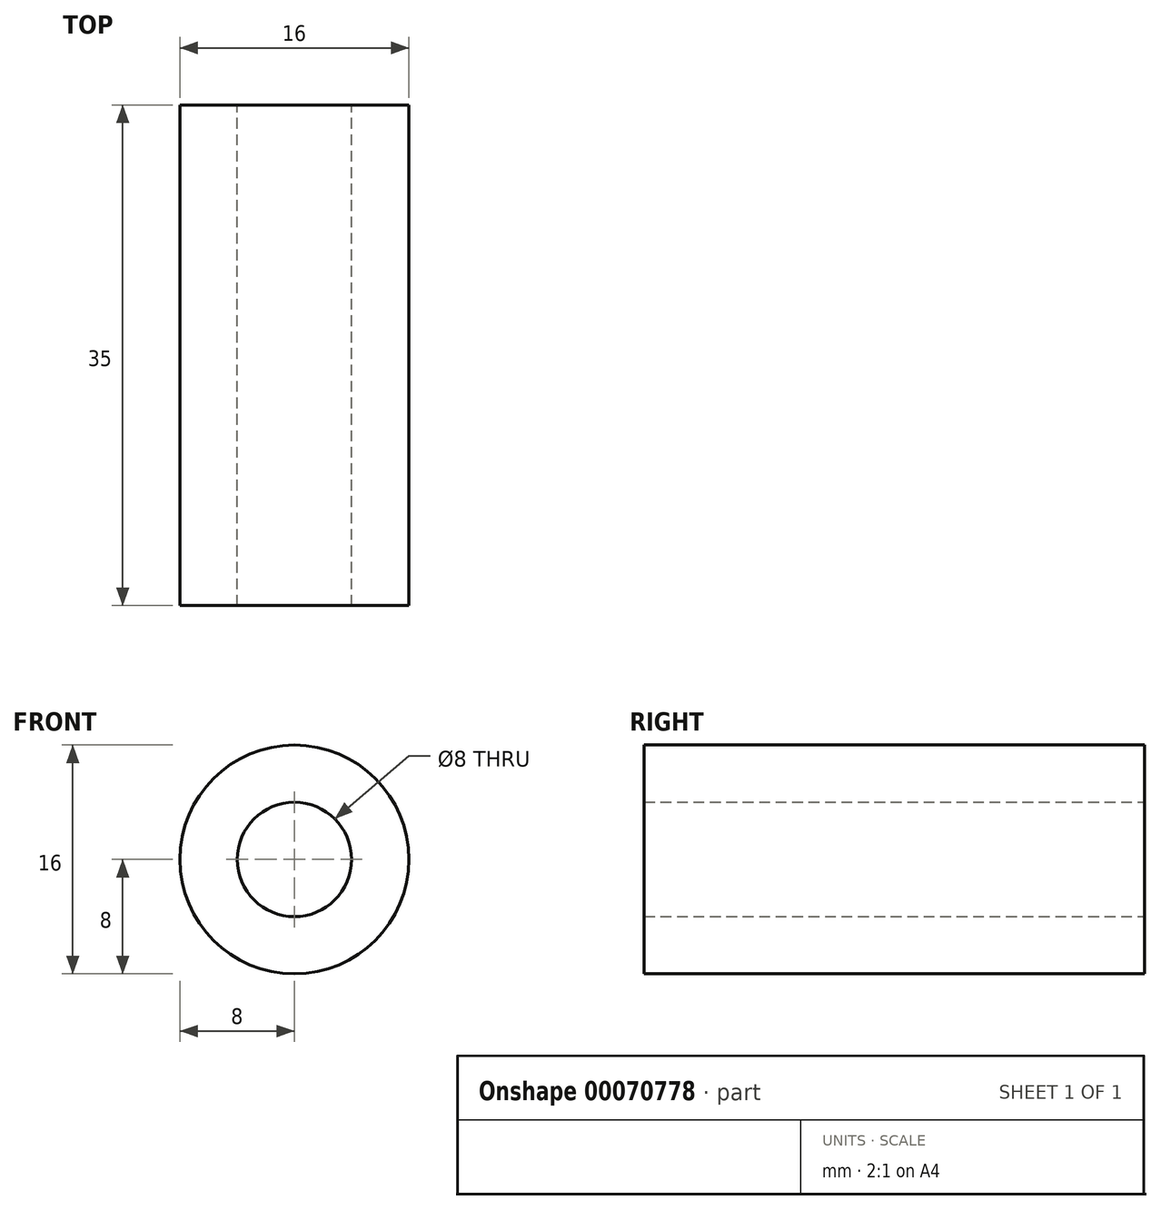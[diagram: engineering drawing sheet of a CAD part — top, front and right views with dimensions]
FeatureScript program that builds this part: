
annotation { "Feature Type Name" : "Feature", "Feature Type Description" : "" }
export const myFeature = defineFeature(function(context is Context, id is Id, definition is map)
    precondition{}
    {
        {
            var Q0;
            Q0=qCreatedBy(makeId("Front.planeOp"),FACE);
            var sketch = newSketch(context, id + "F0", { "sketchPlane" : qUnion([Q0])});
            skCircle(sketch, "E0", {"center": v(0, 0) * mm, "radius": 8 * mm});
            skCircle(sketch, "E1", {"center": v(0, 0) * mm, "radius": 4 * mm});
            skSolve(sketch);
        }
        {
            var Q0;
            Q0 = qSketchRegion(id + "F0", true);
            extrude(context, id + "F1", {"entities" : qUnion([Q0]), "depth" : 35 * mm});
        }
    });
